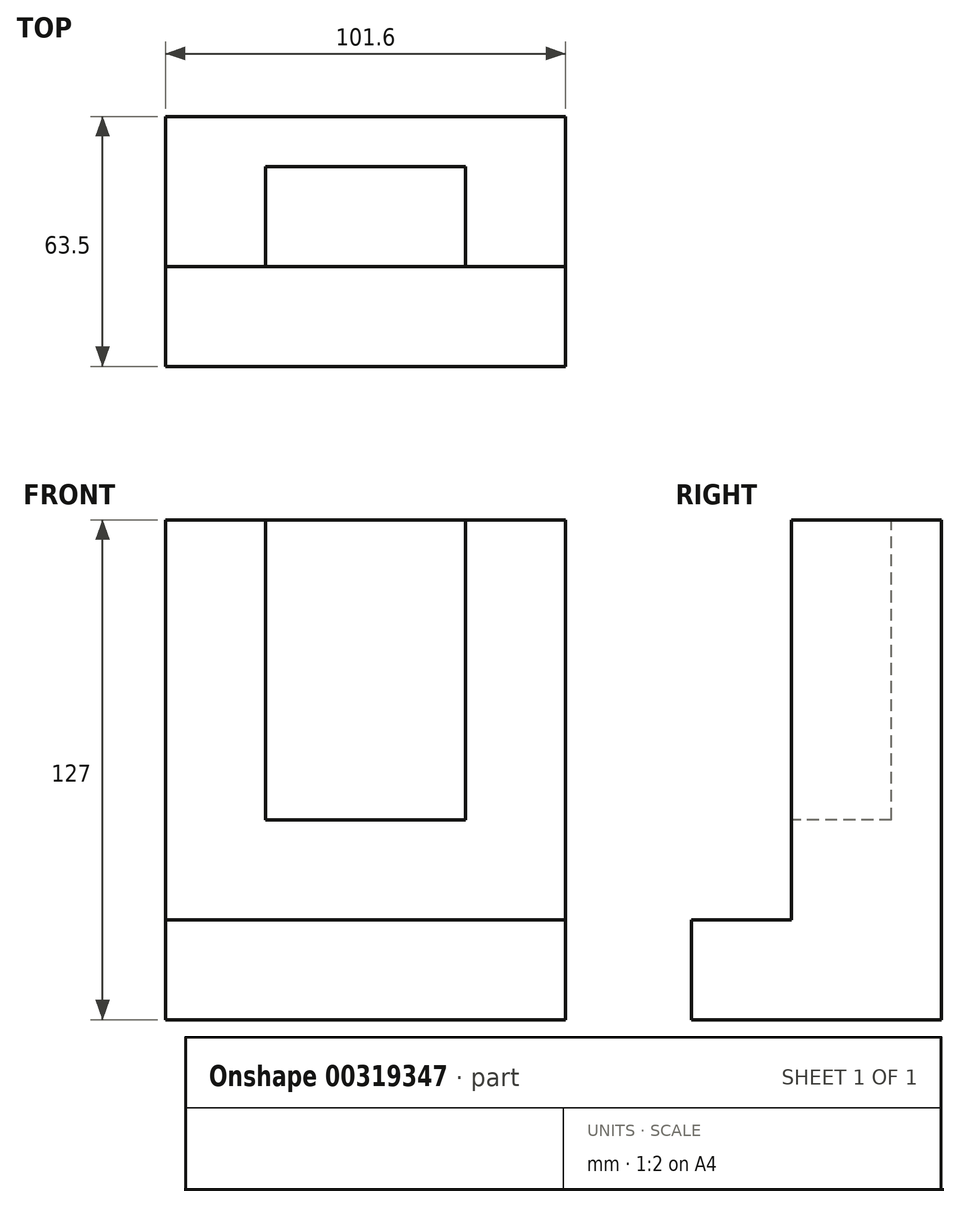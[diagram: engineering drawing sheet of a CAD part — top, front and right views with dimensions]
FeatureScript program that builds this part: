
annotation { "Feature Type Name" : "Feature", "Feature Type Description" : "" }
export const myFeature = defineFeature(function(context is Context, id is Id, definition is map)
    precondition{}
    {
        {
            var Q0;
            Q0=qCreatedBy(makeId("Front.planeOp"),FACE);
            var sketch = newSketch(context, id + "F0", { "sketchPlane" : qUnion([Q0])});
            skLineSegment(sketch, "E0", {"start": v(-60.07, -57.03) * mm, "end": v(41.53, -57.03) * mm});
            skLineSegment(sketch, "E1", {"start": v(41.53, -57.03) * mm, "end": v(41.53, 69.97) * mm});
            skLineSegment(sketch, "E2", {"start": v(41.53, 69.97) * mm, "end": v(-60.07, 69.97) * mm});
            skLineSegment(sketch, "E3", {"start": v(-60.07, 69.97) * mm, "end": v(-60.07, -57.03) * mm});
            skSolve(sketch);
        }
        {
            var Q0;
            Q0=makeQuery(id+"F0.imprint","IMPRINT",FACE,{"disambiguationData":[TD([[makeQuery(id+"F0.imprint","IMPRINT",EDGE,{"derivedFrom":sQuery(id+"F0.wireOp",EDGE,"E0")}),1.0]])]});
            extrude(context, id + "F1", {"entities" : qUnion([Q0]), "depth" : 63.5 * mm});
        }
        {
            var Q0;
            Q0=makeQuery(id+"F1.opExtrude","CAP_FACE",FACE,{"disambiguationData":[OSD([sQuery(id+"F0.wireOp",EDGE,"E0"),sQuery(id+"F0.wireOp",EDGE,"E1"),sQuery(id+"F0.wireOp",EDGE,"E2"),sQuery(id+"F0.wireOp",EDGE,"E3")])],"isStart":false});
            var sketch = newSketch(context, id + "F2", { "sketchPlane" : qUnion([Q0])});
            skLineSegment(sketch, "E4", {"start": v(41.53, -31.63) * mm, "end": v(41.53, 69.97) * mm});
            skLineSegment(sketch, "E5", {"start": v(41.53, 69.97) * mm, "end": v(-60.07, 69.97) * mm});
            skLineSegment(sketch, "E6", {"start": v(-60.07, 69.97) * mm, "end": v(-60.07, -31.63) * mm});
            skLineSegment(sketch, "E7", {"start": v(-60.07, -31.63) * mm, "end": v(41.53, -31.63) * mm});
            skSolve(sketch);
        }
        {
            var Q0;
            Q0=makeQuery(id+"F2.imprint","IMPRINT",FACE,{"disambiguationData":[TD([[makeQuery(id+"F2.imprint","IMPRINT",EDGE,{"derivedFrom":sQuery(id+"F2.wireOp",EDGE,"E4")}),1.0]])]});
            extrude(context, id + "F3", {"entities" : qUnion([Q0]), "operationType" : NewBodyOperationType.REMOVE, "oppositeDirection" : true, "depth" : 25.4 * mm});
        }
        {
            var Q0;
            Q0=makeQuery(id+"F3.boolean.opBoolean","COPY",FACE,{"derivedFrom":makeQuery(id+"F3.opExtrude","CAP_FACE",FACE,{"disambiguationData":[OSD([sQuery(id+"F2.wireOp",EDGE,"E4"),sQuery(id+"F2.wireOp",EDGE,"E5"),sQuery(id+"F2.wireOp",EDGE,"E6"),sQuery(id+"F2.wireOp",EDGE,"E7")])],"isStart":false})});
            var sketch = newSketch(context, id + "F4", { "sketchPlane" : qUnion([Q0])});
            skLineSegment(sketch, "E8", {"start": v(-60.07, -31.63) * mm, "end": v(-60.07, -6.35) * mm});
            skLineSegment(sketch, "E9", {"start": v(-34.67, -6.23) * mm, "end": v(-34.67, 69.97) * mm});
            skLineSegment(sketch, "E10", {"start": v(-34.67, -6.23) * mm, "end": v(16.13, -6.23) * mm});
            skLineSegment(sketch, "E11", {"start": v(16.13, -6.23) * mm, "end": v(16.13, 69.97) * mm});
            skSolve(sketch);
        }
        {
            var Q0;
            {var subQ0=sQuery(id+"F4.wireOp",EDGE,"E9");Q0=makeQuery(id+"F4.imprint","IMPRINT",FACE,{"disambiguationData":[TD([[makeQuery(id+"F4.imprint","IMPRINT",EDGE,{"derivedFrom":subQ0}),-1.0]])]});}
            extrude(context, id + "F5", {"entities" : qUnion([Q0]), "operationType" : NewBodyOperationType.REMOVE, "oppositeDirection" : true, "depth" : 25.4 * mm});
        }
    });
